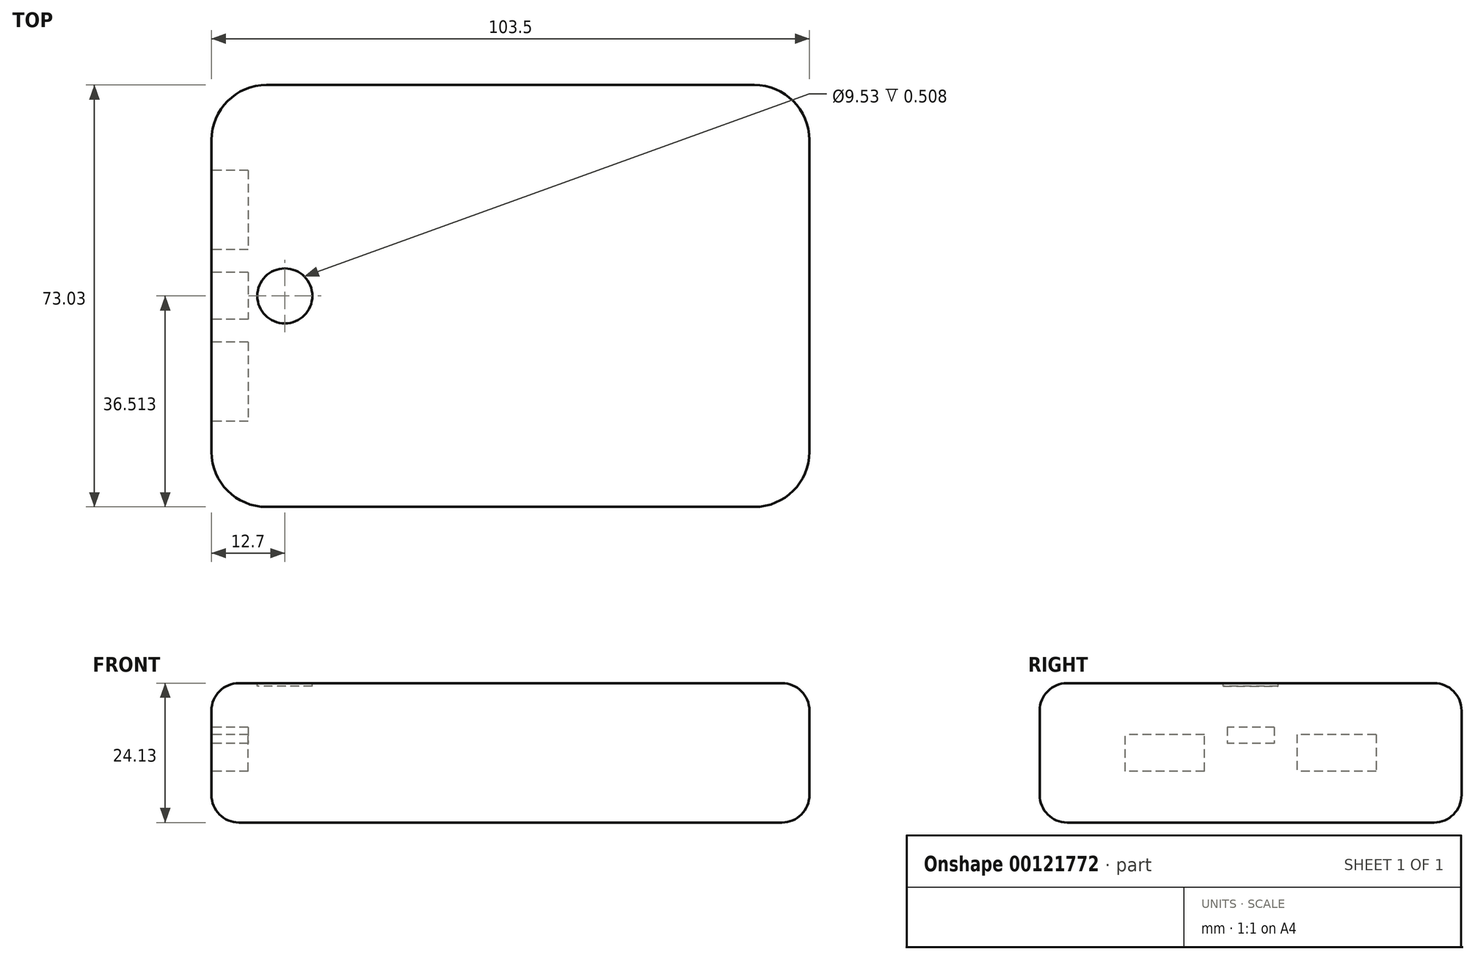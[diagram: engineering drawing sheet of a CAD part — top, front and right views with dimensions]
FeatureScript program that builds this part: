
annotation { "Feature Type Name" : "Feature", "Feature Type Description" : "" }
export const myFeature = defineFeature(function(context is Context, id is Id, definition is map)
    precondition{}
    {
        {
            var Q0;
            Q0=qCreatedBy(makeId("Top.planeOp"),FACE);
            var sketch = newSketch(context, id + "F0", { "sketchPlane" : qUnion([Q0])});
            skLineSegment(sketch, "E0.bottom", {"start": v(9.52, 0) * mm, "end": v(93.98, 0) * mm});
            skLineSegment(sketch, "E0.top", {"start": v(9.52, 73.03) * mm, "end": v(93.98, 73.03) * mm});
            skLineSegment(sketch, "E0.left", {"start": v(0, 9.52) * mm, "end": v(0, 63.5) * mm});
            skLineSegment(sketch, "E0.right", {"start": v(103.5, 9.53) * mm, "end": v(103.5, 63.5) * mm});
            skPoint(sketch, "E1.visualSharp", {"position": v(0, 73.03) * mm});
            skArc(sketch, "E1.filletArc", {"start": v(9.52, 73.03) * mm, "mid": v(2.79, 70.24) * mm, "end": v(0, 63.5) * mm});
            skPoint(sketch, "E2.visualSharp", {"position": v(103.5, 73.03) * mm});
            skArc(sketch, "E2.filletArc", {"start": v(103.5, 63.5) * mm, "mid": v(100.72, 70.24) * mm, "end": v(93.98, 73.03) * mm});
            skPoint(sketch, "E3.visualSharp", {"position": v(103.5, 0) * mm});
            skArc(sketch, "E3.filletArc", {"start": v(93.98, 0) * mm, "mid": v(100.72, 2.79) * mm, "end": v(103.5, 9.53) * mm});
            skPoint(sketch, "E4.visualSharp", {"position": v(0, 0) * mm});
            skArc(sketch, "E4.filletArc", {"start": v(0, 9.52) * mm, "mid": v(2.79, 2.79) * mm, "end": v(9.52, 0) * mm});
            skSolve(sketch);
        }
        {
            var Q0;
            Q0=makeQuery(id+"F0.imprint","IMPRINT",FACE,{"disambiguationData":[TD([[makeQuery(id+"F0.imprint","IMPRINT",EDGE,{"derivedFrom":sQuery(id+"F0.wireOp",EDGE,"E0.bottom")}),1.0]])]});
            extrude(context, id + "F1", {"entities" : qUnion([Q0]), "depth" : 24.13 * mm});
        }
        {
            var Q0;
            Q0=makeQuery(id+"F1.opExtrude","CAP_FACE",FACE,{"disambiguationData":[OSD([sQuery(id+"F0.wireOp",EDGE,"E0.bottom"),sQuery(id+"F0.wireOp",EDGE,"E0.top"),sQuery(id+"F0.wireOp",EDGE,"E0.left"),sQuery(id+"F0.wireOp",EDGE,"E0.right"),sQuery(id+"F0.wireOp",EDGE,"E1.filletArc"),sQuery(id+"F0.wireOp",EDGE,"E2.filletArc"),sQuery(id+"F0.wireOp",EDGE,"E3.filletArc"),sQuery(id+"F0.wireOp",EDGE,"E4.filletArc")])],"isStart":false});
            var Q1;
            Q1=makeQuery(id+"F1.opExtrude","CAP_FACE",FACE,{"disambiguationData":[OSD([sQuery(id+"F0.wireOp",EDGE,"E0.bottom"),sQuery(id+"F0.wireOp",EDGE,"E0.top"),sQuery(id+"F0.wireOp",EDGE,"E0.left"),sQuery(id+"F0.wireOp",EDGE,"E0.right"),sQuery(id+"F0.wireOp",EDGE,"E1.filletArc"),sQuery(id+"F0.wireOp",EDGE,"E2.filletArc"),sQuery(id+"F0.wireOp",EDGE,"E3.filletArc"),sQuery(id+"F0.wireOp",EDGE,"E4.filletArc")])],"isStart":true});
            fillet(context, id + "F2", {"entities" : qUnion([Q0, Q1]), "radius" : 4.76 * mm, "tangentPropagation" : true, "allowEdgeOverflow" : false});
        }
        {
            var Q0;
            Q0=makeQuery(id+"F1.opExtrude","CAP_FACE",FACE,{"disambiguationData":[OSD([sQuery(id+"F0.wireOp",EDGE,"E0.bottom"),sQuery(id+"F0.wireOp",EDGE,"E0.top"),sQuery(id+"F0.wireOp",EDGE,"E0.left"),sQuery(id+"F0.wireOp",EDGE,"E0.right"),sQuery(id+"F0.wireOp",EDGE,"E1.filletArc"),sQuery(id+"F0.wireOp",EDGE,"E2.filletArc"),sQuery(id+"F0.wireOp",EDGE,"E3.filletArc"),sQuery(id+"F0.wireOp",EDGE,"E4.filletArc")])],"isStart":false});
            var sketch = newSketch(context, id + "F3", { "sketchPlane" : qUnion([Q0])});
            skCircle(sketch, "E5", {"center": v(12.7, 36.51) * mm, "radius": 4.76 * mm});
            skPoint(sketch, "E5.centerSnap0", {"position": v(4.76, 36.51) * mm});
            skSolve(sketch);
        }
        {
            var Q0;
            Q0=makeQuery(id+"F3.imprint","IMPRINT",FACE,{"disambiguationData":[TD([[makeQuery(id+"F3.imprint","IMPRINT",EDGE,{"derivedFrom":sQuery(id+"F3.wireOp",EDGE,"E5")}),1.0]])]});
            extrude(context, id + "F4", {"entities" : qUnion([Q0]), "operationType" : NewBodyOperationType.REMOVE, "oppositeDirection" : true, "depth" : 0.5 * mm});
        }
        {
            var Q0;
            Q0=makeQuery(id+"F1.opExtrude","SWEPT_FACE",FACE,{"disambiguationData":[OSD([sQuery(id+"F0.wireOp",EDGE,"E0.left")])]});
            var sketch = newSketch(context, id + "F5", { "sketchPlane" : qUnion([Q0])});
            skLineSegment(sketch, "E6.bottom", {"start": v(-58.23, 15.24) * mm, "end": v(-44.51, 15.24) * mm});
            skLineSegment(sketch, "E6.top", {"start": v(-58.23, 8.9) * mm, "end": v(-44.51, 8.89) * mm});
            skLineSegment(sketch, "E6.left", {"start": v(-58.23, 15.24) * mm, "end": v(-58.23, 8.9) * mm});
            skLineSegment(sketch, "E6.right", {"start": v(-44.51, 15.24) * mm, "end": v(-44.51, 8.89) * mm});
            skLineSegment(sketch, "E7.bottom", {"start": v(-28.51, 8.9) * mm, "end": v(-14.8, 8.9) * mm});
            skLineSegment(sketch, "E7.top", {"start": v(-28.51, 15.24) * mm, "end": v(-14.8, 15.24) * mm});
            skLineSegment(sketch, "E7.left", {"start": v(-28.51, 8.9) * mm, "end": v(-28.51, 15.24) * mm});
            skLineSegment(sketch, "E7.right", {"start": v(-14.8, 8.9) * mm, "end": v(-14.8, 15.24) * mm});
            skLineSegment(sketch, "E8", {"start": v(-58.23, 12.07) * mm, "end": v(-14.8, 12.07) * mm, "construction": true});
            skPoint(sketch, "E9", {"position": v(-36.51, 12.07) * mm});
            skPoint(sketch, "E10", {"position": v(-36.51, 19.37) * mm});
            skPoint(sketch, "E11", {"position": v(-63.5, 12.07) * mm});
            skLineSegment(sketch, "E12.bottom", {"start": v(-40.58, 16.5) * mm, "end": v(-32.45, 16.5) * mm});
            skLineSegment(sketch, "E12.top", {"start": v(-40.58, 13.72) * mm, "end": v(-32.45, 13.72) * mm});
            skLineSegment(sketch, "E12.left", {"start": v(-40.58, 16.5) * mm, "end": v(-40.58, 13.72) * mm});
            skLineSegment(sketch, "E12.right", {"start": v(-32.45, 16.5) * mm, "end": v(-32.45, 13.72) * mm});
            skPoint(sketch, "E13", {"position": v(-36.51, 13.72) * mm});
            skSolve(sketch);
        }
        {
            var Q0;
            Q0=makeQuery(id+"F5.imprint","IMPRINT",FACE,{"disambiguationData":[TD([[makeQuery(id+"F5.imprint","IMPRINT",EDGE,{"derivedFrom":sQuery(id+"F5.wireOp",EDGE,"E6.bottom")}),-1.0]])]});
            var Q1;
            Q1=makeQuery(id+"F5.imprint","IMPRINT",FACE,{"disambiguationData":[TD([[makeQuery(id+"F5.imprint","IMPRINT",EDGE,{"derivedFrom":sQuery(id+"F5.wireOp",EDGE,"E12.bottom")}),-1.0]])]});
            var Q2;
            Q2=makeQuery(id+"F5.imprint","IMPRINT",FACE,{"disambiguationData":[TD([[makeQuery(id+"F5.imprint","IMPRINT",EDGE,{"derivedFrom":sQuery(id+"F5.wireOp",EDGE,"E7.bottom")}),1.0]])]});
            extrude(context, id + "F6", {"entities" : qUnion([Q0, Q1, Q2]), "operationType" : NewBodyOperationType.REMOVE, "oppositeDirection" : true, "depth" : 6.35 * mm});
        }
    });
